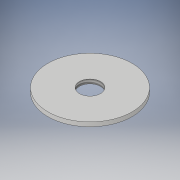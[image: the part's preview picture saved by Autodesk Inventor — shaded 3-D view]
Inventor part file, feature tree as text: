
AUTODESK INVENTOR PART (.ipt)
format: ipt  version: 2019 (Build 230136000, 136)  size: 97,792 bytes
history: native  units: in
note: dims shown in document units (in); Inventor stores cm internally (conversion verified against a paired STEP export)
features: extrude x1, thread x1, sketch x1
ambient origin geometry x8: Origin, YZ Plane, XZ Plane, XY Plane, X Axis, Y Axis, Z Axis, Center Point
bodies: Solid1 (feature_tree)
feature tree (3):
  extrude  "Extrusion1"  Depth=1.0in
  thread  "Thread1"  [1 undecoded]
  sketch  "Sketch1"  dims[d0=0.5in d1=2.0in d2=0.1in d3=0.0in d4=1.0in d5=0.0in]
note: 1 required parameter value undecoded (feature->parameter linkage not recoverable at this tier; creation-order binding heuristic only, values carry confidence <= 0.55)
